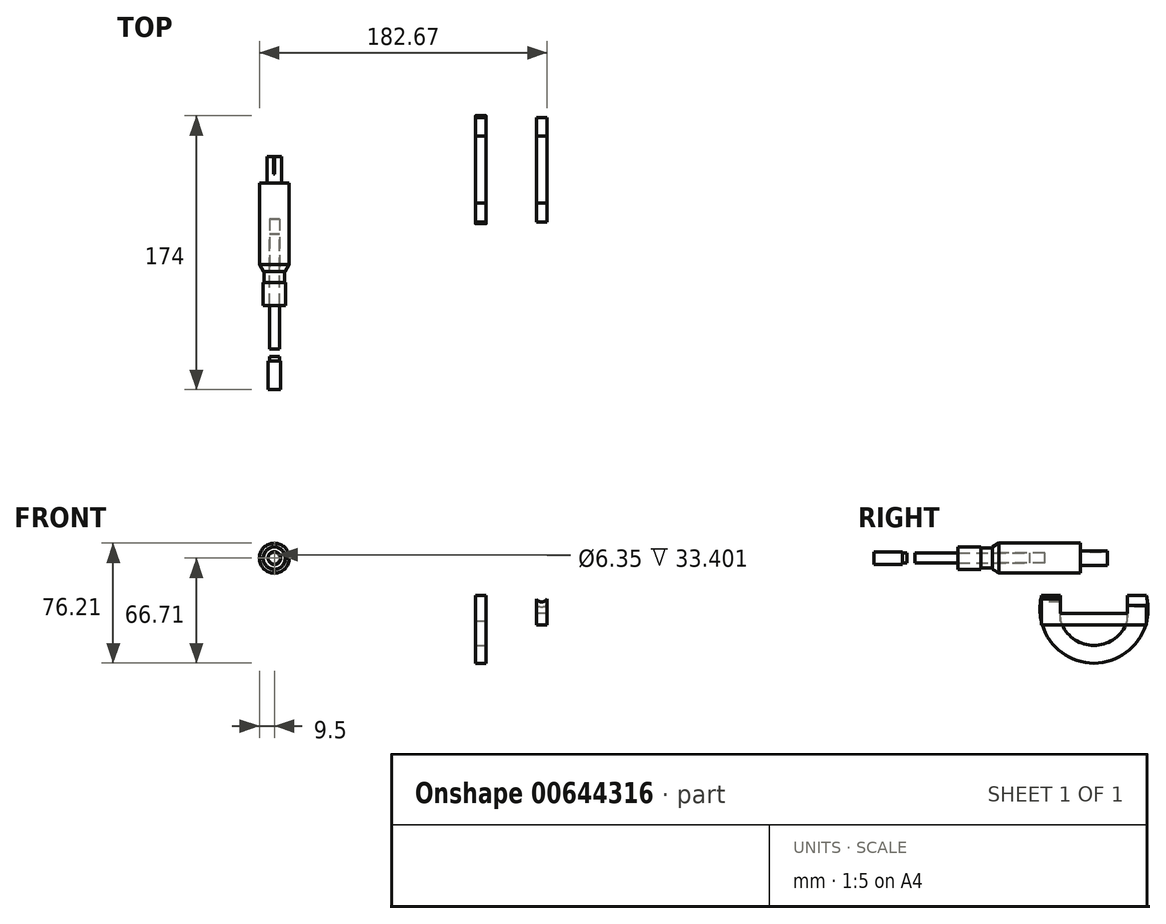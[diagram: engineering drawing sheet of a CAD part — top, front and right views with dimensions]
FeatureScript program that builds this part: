
annotation { "Feature Type Name" : "Feature", "Feature Type Description" : "" }
export const myFeature = defineFeature(function(context is Context, id is Id, definition is map)
    precondition{}
    {
        {
            var Q0;
            Q0=qCreatedBy(makeId("Front.planeOp"),FACE);
            var sketch = newSketch(context, id + "F0", { "sketchPlane" : qUnion([Q0])});
            skCircle(sketch, "E0", {"center": v(0, 0) * mm, "radius": 4.5 * mm});
            skSolve(sketch);
        }
        {
            var Q0;
            Q0=qSketchRegion(id+"F0",true);
            extrude(context, id + "F1", {"entities" : qUnion([Q0]), "depth" : 17 * mm, "offsetDistance" : 25.4 * mm});
        }
        {
            var Q0;
            Q0=makeQuery(id+"F1.opExtrude","CAP_FACE",FACE,{"disambiguationData":[OSD([sQuery(id+"F0.wireOp",EDGE,"E0")])],"isStart":false});
            var sketch = newSketch(context, id + "F2", { "sketchPlane" : qUnion([Q0])});
            skCircle(sketch, "E1", {"center": v(0, 0) * mm, "radius": 9.5 * mm});
            skSolve(sketch);
        }
        {
            var Q0;
            Q0=qSketchRegion(id+"F2",true);
            extrude(context, id + "F3", {"entities" : qUnion([Q0]), "depth" : 56 * mm, "offsetDistance" : 25.4 * mm});
        }
        {
            var Q0;
            Q0=makeQuery(id+"F3.opExtrude","CAP_FACE",FACE,{"disambiguationData":[OSD([sQuery(id+"F2.wireOp",EDGE,"E1")])],"isStart":false});
            var sketch = newSketch(context, id + "F4", { "sketchPlane" : qUnion([Q0])});
            skCircle(sketch, "E2", {"center": v(0, 0) * mm, "radius": 3.17 * mm});
            skSolve(sketch);
        }
        {
            var Q0;
            Q0=qSketchRegion(id+"F4",true);
            extrude(context, id + "F5", {"entities" : qUnion([Q0]), "operationType" : NewBodyOperationType.REMOVE, "oppositeDirection" : true, "depth" : 33.4 * mm, "offsetDistance" : 25.4 * mm});
        }
        {
            var Q0;
            Q0=makeQuery(id+"F3.opExtrude","CAP_FACE",FACE,{"disambiguationData":[OSD([sQuery(id+"F2.wireOp",EDGE,"E1")])],"isStart":false});
            var sketch = newSketch(context, id + "F6", { "sketchPlane" : qUnion([Q0])});
            skCircle(sketch, "E3", {"center": v(0, 0) * mm, "radius": 6.36 * mm});
            skSolve(sketch);
        }
        {
            var Q0;
            Q0=qSketchRegion(id+"F6",true);
            extrude(context, id + "F7", {"entities" : qUnion([Q0]), "operationType" : NewBodyOperationType.ADD, "depth" : 7.2 * mm, "offsetDistance" : 25.4 * mm});
        }
        {
            var Q0;
            Q0=makeQuery(id+"F7.opExtrude","CAP_FACE",FACE,{"disambiguationData":[OSD([sQuery(id+"F6.wireOp",EDGE,"E3")])],"isStart":false});
            var sketch = newSketch(context, id + "F8", { "sketchPlane" : qUnion([Q0])});
            skCircle(sketch, "E4", {"center": v(0, 0) * mm, "radius": 7.1 * mm});
            skSolve(sketch);
        }
        {
            var Q0;
            Q0=qSketchRegion(id+"F8",true);
            extrude(context, id + "F9", {"entities" : qUnion([Q0]), "operationType" : NewBodyOperationType.ADD, "depth" : 14.5 * mm, "offsetDistance" : 25.4 * mm});
        }
        {
            var Q0;
            Q0=qCreatedBy(makeId("Right.planeOp"),FACE);
            cPlane(context, id + "F10", {"entities" : qUnion([Q0]), "cplaneType" : CPlaneType.OFFSET, "offset" : 127.76 * mm, "width" : 152.4 * mm, "height" : 152.4 * mm});
        }
        {
            var Q0;
            Q0=qCreatedBy(id+"F10.planeOp",FACE);
            var sketch = newSketch(context, id + "F11", { "sketchPlane" : qUnion([Q0])});
            skLineSegment(sketch, "E5", {"start": v(24.77, -23.82) * mm, "end": v(-41.65, -23.82) * mm});
            skArc(sketch, "E6", {"start": v(-41.65, -23.82) * mm, "mid": v(-8.44, -66.71) * mm, "end": v(24.77, -23.82) * mm});
            skArc(sketch, "E7", {"start": v(-32.49, -23.82) * mm, "mid": v(-8.59, -53.27) * mm, "end": v(15.31, -23.82) * mm});
            skSolve(sketch);
        }
        {
            var Q0;
            Q0=qSketchRegion(id+"F11",true);
            extrude(context, id + "F12", {"entities" : qUnion([Q0]), "depth" : 6.7 * mm, "offsetDistance" : 25.4 * mm});
        }
        {
            var Q0;
            Q0=makeQuery(id+"F12.opExtrude","CAP_FACE",FACE,{"disambiguationData":[OSD([sQuery(id+"F11.wireOp",EDGE,"E5"),sQuery(id+"F11.wireOp",EDGE,"E6")])],"isStart":false});
            var sketch = newSketch(context, id + "F13", { "sketchPlane" : qUnion([Q0])});
            skLineSegment(sketch, "E8", {"start": v(-29.68, -23.82) * mm, "end": v(-41.65, -23.82) * mm});
            skLineSegment(sketch, "E9", {"start": v(-29.68, -23.82) * mm, "end": v(12.8, -23.82) * mm});
            skLineSegment(sketch, "E10", {"start": v(24.77, -23.82) * mm, "end": v(12.8, -23.82) * mm});
            skLineSegment(sketch, "E11", {"start": v(12.8, -23.82) * mm, "end": v(12.8, -39.76) * mm});
            skLineSegment(sketch, "E12", {"start": v(-29.68, -23.82) * mm, "end": v(-29.68, -39.76) * mm});
            skArc(sketch, "E13", {"start": v(-29.68, -39.76) * mm, "mid": v(-8.44, -55.43) * mm, "end": v(12.8, -39.76) * mm});
            skLineSegment(sketch, "E14", {"start": v(-41.65, -23.82) * mm, "end": v(-29.68, -23.82) * mm});
            skLineSegment(sketch, "E15", {"start": v(12.8, -23.82) * mm, "end": v(24.77, -23.82) * mm});
            skSolve(sketch);
        }
        {
            var Q0;
            Q0=makeQuery(id+"F13.imprint","IMPRINT",FACE,{"disambiguationData":[TD([[makeQuery(id+"F13.imprint","IMPRINT",EDGE,{"derivedFrom":sQuery(id+"F13.wireOp",EDGE,"E9")}),1.0]])]});
            extrude(context, id + "F14", {"entities" : qUnion([Q0]), "operationType" : NewBodyOperationType.REMOVE, "endBound" : BoundingType.UP_TO_NEXT, "oppositeDirection" : true, "depth" : 25.4 * mm, "offsetDistance" : 25.4 * mm});
        }
        {
            var Q0;
            Q0=makeQuery(id+"F3.opExtrude","CAP_EDGE",EDGE,{"disambiguationData":[OSD([sQuery(id+"F2.wireOp",EDGE,"E1")])],"isStart":false});
            chamfer(context, id + "F15", {"entities" : qUnion([Q0]), "chamferType" : ChamferType.OFFSET_ANGLE, "width" : 2.54 * mm, "oppositeDirection" : false, "angle" : 59 * degree, "tangentPropagation" : true});
        }
        {
            var Q0;
            Q0=makeQuery(id+"F1.opExtrude","CAP_FACE",FACE,{"disambiguationData":[OSD([sQuery(id+"F0.wireOp",EDGE,"E0")])],"isStart":true});
            var sketch = newSketch(context, id + "F16", { "sketchPlane" : qUnion([Q0])});
            skLineSegment(sketch, "E16", {"start": v(0, 4.5) * mm, "end": v(0.17, 3.95) * mm});
            skLineSegment(sketch, "E17", {"start": v(0.17, 3.95) * mm, "end": v(0.37, 4.48) * mm});
            skArc(sketch, "E18", {"start": v(0.37, 4.48) * mm, "mid": v(0.19, 4.52) * mm, "end": v(0, 4.5) * mm});
            skSolve(sketch);
        }
        {
            var Q0;
            Q0=qSketchRegion(id+"F16",true);
            var Q1;
            Q1=makeQuery(id+"F3.opExtrude","CAP_FACE",FACE,{"disambiguationData":[OSD([sQuery(id+"F2.wireOp",EDGE,"E1")])],"isStart":true});
            extrude(context, id + "F17", {"entities" : qUnion([Q0]), "operationType" : NewBodyOperationType.REMOVE, "oppositeDirection" : true, "depth" : 11.15 * mm, "endBoundEntityFace" : qUnion([Q1]), "offsetDistance" : 25.4 * mm});
        }
        {
            var Q0;
            Q0=makeQuery(id+"F9.opExtrude","CAP_FACE",FACE,{"disambiguationData":[OSD([sQuery(id+"F8.wireOp",EDGE,"E4")])],"isStart":false});
            var sketch = newSketch(context, id + "F18", { "sketchPlane" : qUnion([Q0])});
            skCircle(sketch, "E19", {"center": v(0, 0) * mm, "radius": 3.17 * mm});
            skSolve(sketch);
        }
        {
            var Q0;
            Q0=qSketchRegion(id+"F18",true);
            extrude(context, id + "F19", {"entities" : qUnion([Q0]), "depth" : 27.5 * mm, "offsetDistance" : 25.4 * mm, "hasSecondDirection" : true, "secondDirectionOppositeDirection" : true, "secondDirectionDepth" : 45.47 * mm});
        }
        {
            var Q0;
            Q0=makeQuery(id+"F19.opExtrude","CAP_FACE",FACE,{"disambiguationData":[OSD([sQuery(id+"F18.wireOp",EDGE,"E19")])],"isStart":false});
            cPlane(context, id + "F20", {"entities" : qUnion([Q0]), "cplaneType" : CPlaneType.OFFSET, "offset" : 5 * mm, "width" : 152.4 * mm, "height" : 152.4 * mm});
        }
        {
            var Q0;
            Q0=qCreatedBy(id+"F20.planeOp",FACE);
            var sketch = newSketch(context, id + "F21", { "sketchPlane" : qUnion([Q0])});
            skCircle(sketch, "E20", {"center": v(0, 0) * mm, "radius": 3.17 * mm});
            skSolve(sketch);
        }
        {
            var Q0;
            Q0=qSketchRegion(id+"F21",true);
            extrude(context, id + "F22", {"entities" : qUnion([Q0]), "depth" : 2.8 * mm, "offsetDistance" : 25.4 * mm});
        }
        {
            var Q0;
            Q0=makeQuery(id+"F22.opExtrude","CAP_FACE",FACE,{"disambiguationData":[OSD([sQuery(id+"F21.wireOp",EDGE,"E20")])],"isStart":false});
            var sketch = newSketch(context, id + "F23", { "sketchPlane" : qUnion([Q0])});
            skCircle(sketch, "E21", {"center": v(0, 0) * mm, "radius": 4 * mm});
            skSolve(sketch);
        }
        {
            var Q0;
            Q0=qSketchRegion(id+"F23",true);
            extrude(context, id + "F24", {"entities" : qUnion([Q0]), "depth" : 18.14 * mm, "offsetDistance" : 25.4 * mm});
        }
        {
            var Q0;
            Q0=makeQuery(id+"F12.opExtrude","CAP_FACE",FACE,{"disambiguationData":[OSD([sQuery(id+"F11.wireOp",EDGE,"E5"),sQuery(id+"F11.wireOp",EDGE,"E6")])],"isStart":false});
            cPlane(context, id + "F25", {"entities" : qUnion([Q0]), "cplaneType" : CPlaneType.OFFSET, "offset" : 32 * mm, "width" : 152.4 * mm, "height" : 152.4 * mm});
        }
        {
            var Q0;
            Q0=qCreatedBy(id+"F25.planeOp",FACE);
            var sketch = newSketch(context, id + "F26", { "sketchPlane" : qUnion([Q0])});
            skLineSegment(sketch, "E22", {"start": v(-41.65, -23.82) * mm, "end": v(-29.68, -23.82) * mm});
            skLineSegment(sketch, "E23", {"start": v(12.8, -23.82) * mm, "end": v(24.77, -23.82) * mm});
            skLineSegment(sketch, "E24", {"start": v(-41.65, -23.82) * mm, "end": v(-41.65, -42.38) * mm});
            skLineSegment(sketch, "E25", {"start": v(-41.65, -42.38) * mm, "end": v(24.77, -42.38) * mm});
            skLineSegment(sketch, "E26", {"start": v(24.77, -42.38) * mm, "end": v(24.77, -23.82) * mm});
            skLineSegment(sketch, "E27", {"start": v(-29.68, -23.82) * mm, "end": v(-29.68, -35.05) * mm});
            skLineSegment(sketch, "E28", {"start": v(-29.68, -35.05) * mm, "end": v(12.8, -35.05) * mm});
            skLineSegment(sketch, "E29", {"start": v(12.8, -35.05) * mm, "end": v(12.8, -23.82) * mm});
            skSolve(sketch);
        }
        {
            var Q0;
            Q0 = qSketchRegion(id + "F26", true);
            extrude(context, id + "F27", {"entities" : qUnion([Q0]), "depth" : 6.7 * mm, "offsetDistance" : 25.4 * mm});
        }
        {
            var Q0;
            Q0=makeQuery(id+"F27.opExtrude","SWEPT_FACE",FACE,{"disambiguationData":[OSD([sQuery(id+"F26.wireOp",EDGE,"E24")])]});
            var sketch = newSketch(context, id + "F28", { "sketchPlane" : qUnion([Q0])});
            skCircle(sketch, "E30", {"center": v(169.82, -23.82) * mm, "radius": 4 * mm});
            skSolve(sketch);
        }
        {
            var Q0;
            Q0 = qSketchRegion(id + "F28", true);
            extrude(context, id + "F29", {"entities" : qUnion([Q0]), "operationType" : NewBodyOperationType.REMOVE, "oppositeDirection" : true, "depth" : 12.83 * mm, "offsetDistance" : 25.4 * mm});
        }
        {
            var Q0;
            Q0=makeQuery(id+"F27.opExtrude","SWEPT_FACE",FACE,{"disambiguationData":[OSD([sQuery(id+"F26.wireOp",EDGE,"E29")])]});
            var sketch = newSketch(context, id + "F30", { "sketchPlane" : qUnion([Q0])});
            skCircle(sketch, "E31", {"center": v(169.82, -23.82) * mm, "radius": 7.1 * mm});
            skSolve(sketch);
        }
        {
            var Q0;
            Q0 = qSketchRegion(id + "F30", true);
            extrude(context, id + "F31", {"entities" : qUnion([Q0]), "operationType" : NewBodyOperationType.REMOVE, "oppositeDirection" : true, "depth" : 19 * mm, "offsetDistance" : 25.4 * mm});
        }
    });
